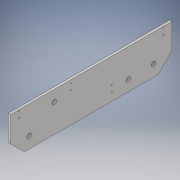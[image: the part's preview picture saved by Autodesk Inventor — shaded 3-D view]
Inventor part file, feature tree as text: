
AUTODESK INVENTOR PART (.ipt)
format: ipt  version: 2017 (Build 210142000, 142)  size: 174,080 bytes
history: native  units: in
note: dims shown in document units (in); Inventor stores cm internally (conversion verified against a paired STEP export)
features: extrude x4, sketch x4, projected_geometry x3, chamfer x2
ambient origin geometry x8: Origin, YZ Plane, XZ Plane, XY Plane, X Axis, Y Axis, Z Axis, Center Point
bodies: Solid1 (feature_tree)
feature tree (13):
  extrude  "Extrusion1"  Depth=17.5in
  chamfer  "Chamfer1"  Distance=2.0in
  chamfer  "Chamfer2"  Distance=0.25in
  extrude  "Extrusion2"  Depth=0.25in TaperAngle=45.0deg
  extrude  "Extrusion3"  Depth=0.25in TaperAngle=45.0deg
  extrude  "Extrusion5"  Depth=0.25in
  sketch  "Sketch1"  dims[d0=4.25in d1=17.5in]
  sketch  "Sketch2"  dims[d2=0.501in]
  projected_geometry  "Projected Loop1"
  sketch  "Sketch3"  dims[d3=1.25in]
  projected_geometry  "Projected Loop2"
  sketch  "Sketch5"  dims[d4=2.0in d5=2.0in d6=0.25in d7=0.0in d8=1.5in d9=0.125in d10=45.0deg d11=1.5in d12=0.125in d13=45.0deg d14=0.501in d15=4.741in d16=1.181in d17=0.501in d18=1.181in d19=4.741in d20=1.0in d21=0.0in d22=6.517in d23=0.125in d24=0.603in d25=0.125in d26=0.63in d27=6.517in d28=0.125in d29=0.603in d30=6.517in d31=0.125in d32=0.63in d33=6.517in d34=0.125in d35=6.517in d36=0.315in d37=0.125in d38=0.63in d39=0.125in d40=0.125in d41=0.9in d42=0.63in d43=6.517in d44=1.0in d45=0.0in d59=0.155in d60=0.906in d61=0.094in d62=0.155in d64=0.155in d65=0.155in d66=0.094in d68=0.904in d69=1.0in d70=0.0in d71=0.781in d72=0.781in]
  projected_geometry  "Projected Loop4"
